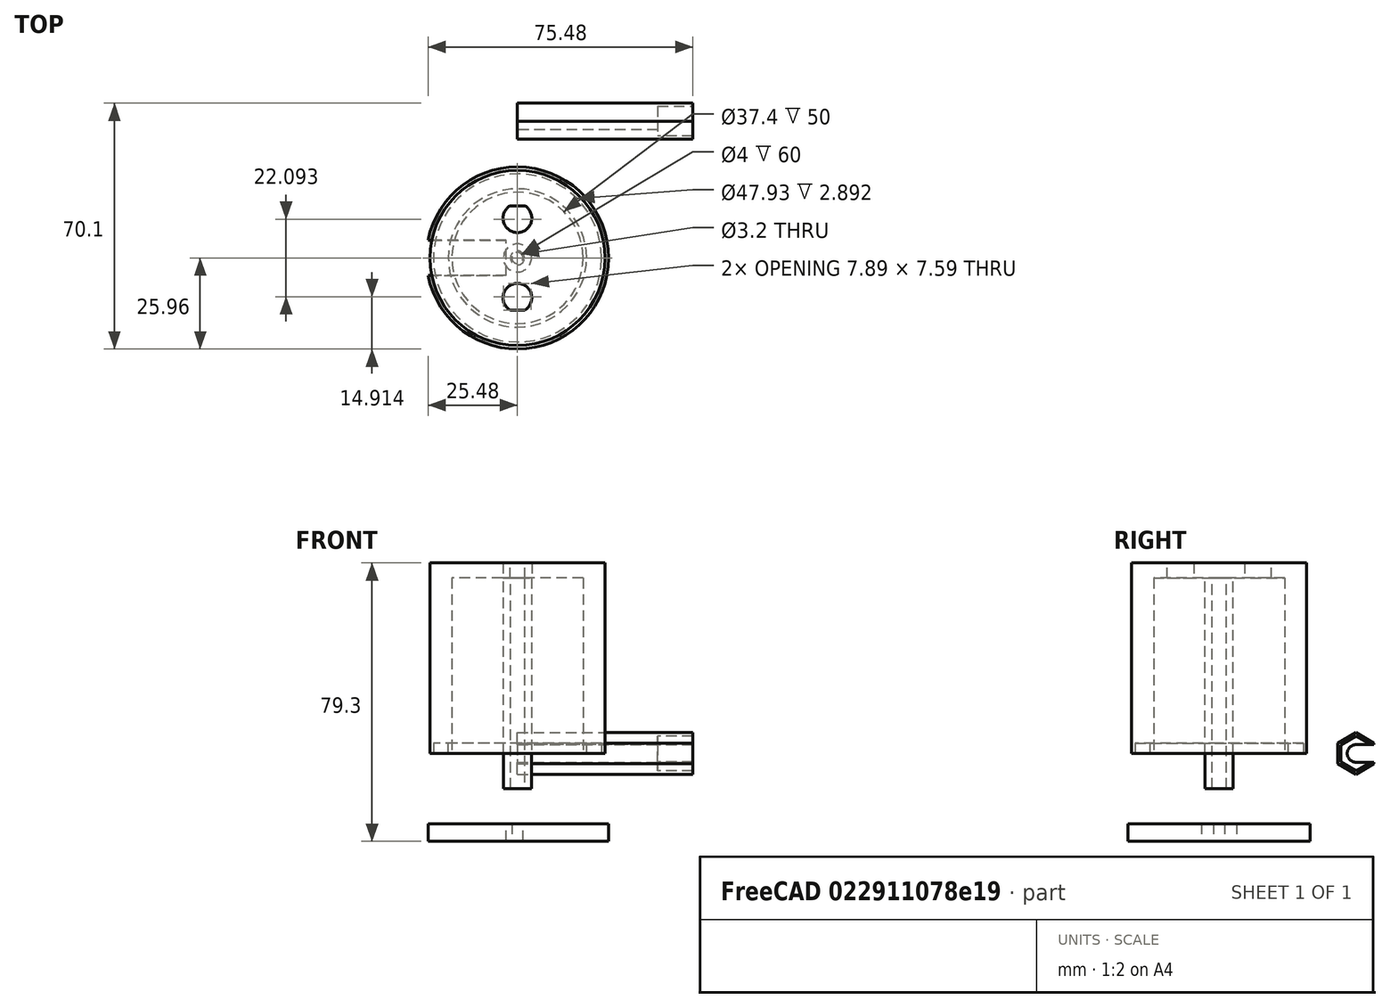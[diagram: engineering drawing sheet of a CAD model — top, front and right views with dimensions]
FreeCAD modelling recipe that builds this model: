
FCSTD DOCUMENT  (FreeCAD 0.18.4R)
Label: sealedadaptor
License: All rights reserved
LicenseURL: http://en.wikipedia.org/wiki/All_rights_reserved
objects: TechDraw::DrawViewDimension×10, Sketcher::SketchObject×8, Spreadsheet::Sheet×6, TechDraw::DrawViewPart×6, PartDesign::Pocket×4, PartDesign::Plane×3, PartDesign::Pad×3, PartDesign::Body×3, Part::Feature×2, PartDesign::Revolution×1, PartDesign::PolarPattern×1, TechDraw::DrawSVGTemplate×1, TechDraw::DrawViewAnnotation×1, TechDraw::DrawPage×1
note: 33 computed .brp shape members not serialized (recipe doc carries the construction recipe); baked Part::Feature solids carry a one-line shape summary decoded from their .brp

FEATURE [Spreadsheet::Sheet] Spreadsheet  label="conn"
  cells = A1=cutout_diam; B1==8mm; A2=cutout_slot_offset; B2==3.6mm; A3=separation; B3==conn.B5 + 1mm; A4=x_shift; B4==22.23mm - 13.97mm; A5=max_diam; B5==12.7mm; A6=max_thick; B6==4.3mm; A7=offset_from_wall; B7==1mm; A8=number connectors; B8=2
FEATURE [Spreadsheet::Sheet] Spreadsheet001  label="oring"
  cells = A1=gland_width; B1==0.16 * 25.4mm; C1=Oring #223; A2=gland_depth; B2==0.106 * 25.4mm; A3=gland_OD; B3==1.887 * 25.4mm
FEATURE [Spreadsheet::Sheet] Spreadsheet002  label="dimz"
  cells = A1=nutspace_height; B1==15mm; A2=nutspace_width; B2==0.4 * 25.4mm; A3=Screw diam; B3==0.25 * 25.4mm + 1mm; A4=box_height; B4==50mm; A5=oring_wall; B5==1mm; A6=plate_thick; B6==5mm; A9=track_width; B9==10mm; A11=internal_diameter; B11==oring.B3 / 2 - oring.B1 - dimz.B5; A12=screwpillar_overextent; B12==10mm; A13=insert hole diam; B13==4mm; A14=separate insert pilars; B14==12mm; A16=screw_hole_bottomdiam; B16==3.2mm
FEATURE [Sketcher::SketchObject] Sketch  label="oring and base struct"
  MapMode = 5
  Placement = pos=(0,0,0) rot=(1,0,0;1.5708rad)
  Support = -> [XZ_Plane]
  expr: Constraints[27] = dimz.B4
  expr: Constraints[29] = conn.B6
  expr: Constraints[26] = dimz.B5
  expr: Constraints[28] = oring.B3 / 2
  expr: Constraints[25] = oring.B2 + tol.B1
  expr: Constraints[24] = oring.B1 + tol.B1
  sketch-geometry (10):
    g0: LineSegment StartX=0 StartY=54.3 StartZ=0 EndX=0 EndY=50 EndZ=0
    g1: LineSegment StartX=0 StartY=50 StartZ=0 EndX=18.7009 EndY=50 EndZ=0
    g2: LineSegment StartX=18.7009 StartY=50 StartZ=0 EndX=18.7009 EndY=0 EndZ=0
    g3: LineSegment StartX=18.7009 StartY=0 StartZ=0 EndX=19.7009 EndY=0 EndZ=0
    g4: LineSegment StartX=19.7009 StartY=0 StartZ=0 EndX=19.7009 EndY=2.8924 EndZ=0
    g5: LineSegment StartX=19.7009 StartY=2.8924 StartZ=0 EndX=23.9649 EndY=2.8924 EndZ=0
    g6: LineSegment StartX=23.9649 StartY=2.8924 StartZ=0 EndX=23.9649 EndY=0 EndZ=0
    g7: LineSegment StartX=23.9649 StartY=0 StartZ=0 EndX=24.9649 EndY=0 EndZ=0
    g8: LineSegment StartX=24.9649 StartY=0 StartZ=0 EndX=24.9649 EndY=54.3 EndZ=0
    g9: LineSegment StartX=24.9649 StartY=54.3 StartZ=0 EndX=0 EndY=54.3 EndZ=0
  constraints (30):
    c: Coincident(g0,g1)
    c: Coincident(g1,g2)
    c: Coincident(g2,g3)
    c: Coincident(g3,g4)
    c: Coincident(g4,g5)
    c: Coincident(g5,g6)
    c: Coincident(g6,g7)
    c: Coincident(g7,g8)
    c: Coincident(g8,g9)
    c: Coincident(g9,g0)
    c: Parallel(g0,g2)
    c: Parallel(g2,g4)
    c: Parallel(g4,g6)
    c: Parallel(g6,g8)
    c: Parallel(g8,g-2)
    c: Parallel(g1,g9)
    c: Parallel(g9,g5)
    c: Parallel(g5,g3)
    c: Parallel(g3,g7)
    c: Parallel(g3,g-1)
    c: PointOnObject(g0,g-2)
    c: PointOnObject(g2,g-1)
    c: Equal(g7,g3)
    c: Equal(g6,g4)
    c: DistanceX(g5,g5) = 4.264
    c: DistanceY(g4,g4) = 2.8924
    c: DistanceX(g3,g3) = 1
    c: DistanceY(g-1,g0) = 50
    c: DistanceX(g-1,g6) = 23.9649
    c: DistanceY(g0,g0) = 4.3
FEATURE [PartDesign::Revolution] Revolution  label="base_structure"
  Angle = 360
  Axis = (0,-2e-16,1)
  Base = (0,0,0)
  Placement = pos=(0,0,0) rot=(1,0,0;1.5708rad)
  Profile = -> Sketch
  ReferenceAxis = -> Sketch [V_Axis]
  Reversed = true
FEATURE [Spreadsheet::Sheet] Spreadsheet003  label="tol"
  cells = A1=inplane; B1==0.2mm
FEATURE [PartDesign::Plane] DatumPlane  label="bottom_face"
  AttachmentOffset = pos=(0,0,-50) rot=(0,0,1;0rad)
  Length = 59.9158
  MapMode = 3
  Placement = pos=(0,1.11e-14,50) rot=(1,0,0;3.14159rad)
  ResizeMode = 0
  Support = -> [Revolution]
  Width = 59.9158
  expr: AttachmentOffset.Base.z = -dimz.B4
FEATURE [Sketcher::SketchObject] Sketch001  label="cutout_conn"
  MapMode = 5
  Placement = pos=(0,1.11e-14,50) rot=(1,0,0;3.14159rad)
  Support = -> [DatumPlane]
  expr: Constraints[6] = dimz.B11 - conn.B5 / 2 - tol.B1 - conn.B7
  expr: Constraints[5] = 360deg - acos(conn.B2 / conn.B1)
  expr: Constraints[4] = conn.B1 / 2 + tol.B1 / 2
  sketch-geometry (2):
    g0: ArcOfCircle CenterX=0 CenterY=11.3509 CenterZ=0 NormalX=0 NormalY=0 NormalZ=1 AngleXU=0 Radius=4.1 StartAngle=2.12281 EndAngle=7.30197
    g1: LineSegment StartX=-2.15006 StartY=14.8419 StartZ=0 EndX=2.15006 EndY=14.8419 EndZ=0
  constraints (7):
    c: Coincident(g1,g0)
    c: Coincident(g1,g0)
    c: PointOnObject(g0,g-2)
    c: Perpendicular(g-2,g1)
    c: Radius(g0) = 4.1
    c: Angle(g0) = 5.17915
    c: DistanceY(g-1,g0) = 11.3509
FEATURE [PartDesign::Pocket] Pocket  label="conn_hole"
  BaseFeature = -> Revolution
  Length = 5
  Length2 = 100
  Placement = pos=(0,0,0) rot=(1,0,0;1.5708rad)
  Profile = -> Sketch001
  Type = 1
FEATURE [PartDesign::PolarPattern] PolarPattern  label="repeating_connholes"
  Angle = 360
  Axis = -> Sketch001 [N_Axis]
  BaseFeature = -> Pocket
  Occurrences = 2
  Originals = -> [Pocket]
  Placement = pos=(0,0,0) rot=(1,0,0;1.5708rad)
  expr: Occurrences = conn.B8
FEATURE [Sketcher::SketchObject] Sketch002
  MapMode = 5
  Placement = pos=(0,1.11e-14,50) rot=(1,0,0;3.14159rad)
  Support = -> [DatumPlane]
  expr: Constraints[4] = 0
  expr: Constraints[3] = dimz.B13 / 2
  expr: Constraints[1] = dimz.B13
  sketch-geometry (2):
    g0: Circle CenterX=0 CenterY=0 CenterZ=0 NormalX=0 NormalY=0 NormalZ=1 AngleXU=0 Radius=4
    g1: Circle CenterX=0 CenterY=0 CenterZ=0 NormalX=0 NormalY=0 NormalZ=1 AngleXU=0 Radius=2
  constraints (5):
    c: PointOnObject(g0,g-1)
    c: Radius(g0) = 4
    c: Coincident(g1,g0)
    c: Radius(g1) = 2
    c: DistanceX(g-1,g0) = 0
FEATURE [PartDesign::Pad] Pad  label="screw_pillar"
  BaseFeature = -> PolarPattern
  Length = 60
  Length2 = 100
  Placement = pos=(0,0,0) rot=(1,0,0;1.5708rad)
  Profile = -> Sketch002
  Type = 0
  expr: Length = dimz.B4 + dimz.B12
FEATURE [PartDesign::Body] Body  label="top"
  Group = -> [Sketch,Revolution,DatumPlane,Sketch001,Pocket,PolarPattern,Sketch002,Pad]
  Origin = -> Origin
  Tip = -> Pad
FEATURE [Part::Feature] Part__Feature  label="connector1"
  Placement = pos=(0,11.3509,41.74) rot=(0,-1,0;1.5708rad)
  shape: bbox 12.7 x 12.7 x 22.23 mm, 134 faces, 0 solids (baked)
  expr: Placement.Base.y = dimz.B11 - conn.B5 / 2 - tol.B1 - conn.B7
  expr: Placement.Base.z = dimz.B4 - (22.23mm - 13.97mm)
FEATURE [Part::Feature] Part__Feature001  label="connector2"
  Placement = pos=(0,-11.3509,41.74) rot=(0,-1,0;1.5708rad)
  shape: bbox 12.7 x 12.7 x 22.23 mm, 134 faces, 0 solids (baked)
  expr: Placement.Base.y = -(dimz.B11 - conn.B5 / 2 - tol.B1 - conn.B7)
  expr: Placement.Base.z = dimz.B4 - (22.23mm - 13.97mm)
FEATURE [Sketcher::SketchObject] Sketch003
  MapMode = 5
  Support = -> [XY_Plane001]
  expr: Constraints[0] = oring.B3 / 2 + 2 * dimz.B5
  sketch-geometry (1):
    g0: Circle CenterX=0 CenterY=0 CenterZ=0 NormalX=0 NormalY=0 NormalZ=1 AngleXU=0 Radius=25.9649
  constraints (2):
    c: Radius(g0) = 25.9649
    c: Coincident(g-1,g0)
FEATURE [PartDesign::Pad] Pad001
  Length = 5
  Length2 = 100
  Profile = -> Sketch003
  Type = 0
  expr: Length = dimz.B6
FEATURE [Sketcher::SketchObject] Sketch004
  MapMode = 5
  Placement = pos=(0,0,0) rot=(1,0,0;3.14159rad)
  Support = -> [Pad001]
  expr: Constraints[11] = dimz.B16
  expr: Constraints[9] = dimz.B9
  expr: Constraints[12] = oring.B3 / 2 + oring.B1 + 2 * dimz.B5
  expr: Constraints[1] = dimz.B16 / 2
  sketch-geometry (5):
    g0: Circle CenterX=0 CenterY=0 CenterZ=0 NormalX=0 NormalY=0 NormalZ=1 AngleXU=0 Radius=1.6
    g1: LineSegment StartX=-30.0289 StartY=5 StartZ=0 EndX=-3.2 EndY=5 EndZ=0
    g2: LineSegment StartX=-3.2 StartY=5 StartZ=0 EndX=-3.2 EndY=-5 EndZ=0
    g3: LineSegment StartX=-3.2 StartY=-5 StartZ=0 EndX=-30.0289 EndY=-5 EndZ=0
    g4: LineSegment StartX=-30.0289 StartY=-5 StartZ=0 EndX=-30.0289 EndY=5 EndZ=0
  constraints (13):
    c: Coincident(g0,g-1)
    c: Radius(g0) = 1.6
    c: Coincident(g1,g2)
    c: Coincident(g2,g3)
    c: Coincident(g3,g4)
    c: Coincident(g4,g1)
    c: Horizontal(g1)
    c: Horizontal(g3)
    c: Vertical(g4)
    c: DistanceY(g2,g2) = 10
    c: Symmetric(g1,g2,g-1)
    c: DistanceX(g1,g-1) = 3.2
    c: DistanceX(g3,g-1) = 30.0289
FEATURE [PartDesign::Pocket] Pocket001
  BaseFeature = -> Pad001
  Length = 5
  Length2 = 100
  Profile = -> Sketch004
  Type = 1
FEATURE [PartDesign::Body] Body001  label="bottom"
  Group = -> [Sketch003,Pad001,Sketch004,Pocket001]
  Origin = -> Origin001
  Placement = pos=(0,0,-25) rot=(0,0,1;0rad)
  Tip = -> Pocket001
FEATURE [TechDraw::DrawSVGTemplate] Template
  EditableTexts = Designed_by_Name=Félix Thouin; Drawing_number=1; FC-Date=2021-02-09; FC-SC=1; FC-SH=1; FC-Title=Sealed adapter; Subtitle=For FTIR signal feedthrough; Weight=30g
  Height = 210
  Orientation = 1
  Width = 297
FEATURE [TechDraw::DrawViewPart] View
  CoarseView = false
  Direction = (1,0,0)
  Focus = 100
  HardHidden = false
  IsoCount = 0
  IsoHidden = false
  IsoVisible = false
  LockPosition = false
  Perspective = false
  Rotation = 0
  ScaleType = 0
  SeamHidden = false
  SeamVisible = false
  SmoothHidden = false
  SmoothVisible = false
  Source = -> [Body]
  X = 52.5647
  Y = 150.576
FEATURE [TechDraw::DrawViewPart] View001
  CoarseView = false
  Direction = (0,0,-1)
  Focus = 100
  HardHidden = false
  IsoCount = 0
  IsoHidden = false
  IsoVisible = false
  LockPosition = false
  Perspective = false
  Rotation = 0
  ScaleType = 0
  SeamHidden = false
  SeamVisible = false
  SmoothHidden = false
  SmoothVisible = false
  Source = -> [Body]
  X = 126.594
  Y = 154.604
FEATURE [TechDraw::DrawViewPart] View002
  CoarseView = false
  Direction = (0.354,-0.354,-0.866)
  Focus = 100
  HardHidden = false
  IsoCount = 0
  IsoHidden = false
  IsoVisible = false
  LockPosition = false
  Perspective = false
  Rotation = 0
  ScaleType = 0
  SeamHidden = false
  SeamVisible = false
  SmoothHidden = false
  SmoothVisible = false
  Source = -> [Body]
  X = 215.73
  Y = 153.597
FEATURE [Sketcher::SketchObject] Sketch008
  MapMode = 5
  Placement = pos=(0,0,0) rot=(0.57735,0.57735,0.57735;2.0944rad)
  Support = -> [YZ_Plane002]
  expr: Constraints[19] = (dimztool.B2 + tol.B1 + dimztool.B3) / 2
  sketch-geometry (7):
    g0: LineSegment StartX=5.13986 StartY=-2.9675 StartZ=0 EndX=5.13986 EndY=2.9675 EndZ=0
    g1: LineSegment StartX=5.13986 StartY=2.9675 StartZ=0 EndX=0 EndY=5.935 EndZ=0
    g2: LineSegment StartX=0 StartY=5.935 StartZ=0 EndX=-5.13986 EndY=2.9675 EndZ=0
    g3: LineSegment StartX=-5.13986 StartY=2.9675 StartZ=0 EndX=-5.13986 EndY=-2.9675 EndZ=0
    g4: LineSegment StartX=-5.13986 StartY=-2.9675 StartZ=0 EndX=0 EndY=-5.935 EndZ=0
    g5: LineSegment StartX=-4e-16 StartY=-5.935 StartZ=0 EndX=5.13986 EndY=-2.9675 EndZ=0
    g6: Circle [constr] CenterX=0 CenterY=0 CenterZ=0 NormalX=0 NormalY=0 NormalZ=1 AngleXU=0 Radius=5.935
  constraints (16):
    c: Coincident(g0,g1)
    c: Coincident(g1,g2)
    c: Coincident(g2,g3)
    c: Coincident(g3,g4)
    c: Coincident(g4,g5)
    c: Coincident(g5,g0)
    c: Equal(g0, g1-g5) x5
    c: PointOnObject(g0,g6)
    c: PointOnObject(g1,g6)
    c: PointOnObject(g2,g6)
    c: PointOnObject(g3,g6)
    c: PointOnObject(g4,g6)
    c: PointOnObject(g5,g6)
    c: Coincident(g6,g-1)
    c: PointOnObject(g1,g-2)
    c: Radius(g6) = 5.935
FEATURE [Spreadsheet::Sheet] Spreadsheet004  label="dimztool"
  cells = A1=height; B1==50mm; A2=sma_dist_apex; B2==9.67mm; A3=extra_thick; B3==2mm; A4=depth; B4==10mm; A5=cable_diam; B5==5mm
FEATURE [PartDesign::Pad] Pad002
  Length = 50
  Length2 = 100
  Placement = pos=(0,0,0) rot=(0.57735,0.57735,0.57735;2.0944rad)
  Profile = -> Sketch008
  Type = 0
  expr: Length = dimztool.B1
FEATURE [Spreadsheet::Sheet] Spreadsheet005  label="tol001"
  cells = A1=in plane tol; B1==0.2mm
FEATURE [PartDesign::Plane] DatumPlane002  label="cabletrench_datum"
  Length = 24
  MapMode = 2
  Placement = pos=(0,0,0) rot=(0.57735,0.57735,0.57735;2.0944rad)
  ResizeMode = 0
  Support = -> [Pad002]
  Width = 24
FEATURE [Sketcher::SketchObject] Sketch009
  MapMode = 5
  Placement = pos=(0,0,0) rot=(0.57735,0.57735,0.57735;2.0944rad)
  Support = -> [DatumPlane002]
  expr: Constraints[10] = dimztool.B5
  expr: Constraints[7] = dimztool.B5 / 2
  sketch-geometry (4):
    g0: ArcOfCircle CenterX=0 CenterY=0 CenterZ=0 NormalX=0 NormalY=0 NormalZ=1 AngleXU=0 Radius=2.5 StartAngle=1.5708 EndAngle=4.71239
    g1: LineSegment StartX=2.22264e-08 StartY=2.5 StartZ=0 EndX=9.19793 EndY=2.5 EndZ=0
    g2: LineSegment StartX=9.19793 StartY=2.5 StartZ=0 EndX=9.19793 EndY=-2.5 EndZ=0
    g3: LineSegment StartX=9.19793 StartY=-2.5 StartZ=0 EndX=2.22264e-08 EndY=-2.5 EndZ=0
  constraints (11):
    c: Coincident(g0,g-1)
    c: Coincident(g1,g2)
    c: Coincident(g2,g3)
    c: Coincident(g1,g0)
    c: Coincident(g3,g0)
    c: Parallel(g1,g-1)
    c: Parallel(g3,g-1)
    c: Radius(g0) = 2.5
    c: DistanceX(g0,g0) = 0
    c: Symmetric(g2,g1,g-1)
    c: DistanceY(g2,g2) = 5
FEATURE [PartDesign::Pocket] Pocket005  label="cabletrench"
  BaseFeature = -> Pad002
  Length = 5
  Length2 = 100
  Placement = pos=(0,0,0) rot=(0.57735,0.57735,0.57735;2.0944rad)
  Profile = -> Sketch009
  Reversed = true
  Type = 1
FEATURE [PartDesign::Plane] DatumPlane003  label="wrench_datum"
  AttachmentOffset = pos=(0,0,50) rot=(0,0,1;0rad)
  Length = 24
  MapMode = 2
  Placement = pos=(50,0,0) rot=(0.57735,0.57735,0.57735;2.0944rad)
  ResizeMode = 0
  Support = -> [Pocket005]
  Width = 24
  expr: AttachmentOffset.Base.z = dimztool.B1
FEATURE [Sketcher::SketchObject] Sketch010
  MapMode = 5
  Placement = pos=(50,0,0) rot=(0.57735,0.57735,0.57735;2.0944rad)
  Support = -> [DatumPlane003]
  expr: Constraints[19] = dimztool.B2 + tol.B1
  sketch-geometry (7):
    g0: LineSegment StartX=4.27384 StartY=2.4675 StartZ=0 EndX=0 EndY=4.935 EndZ=0
    g1: LineSegment StartX=0 StartY=4.935 StartZ=0 EndX=-4.27384 EndY=2.4675 EndZ=0
    g2: LineSegment StartX=-4.27384 StartY=2.4675 StartZ=0 EndX=-4.27384 EndY=-2.4675 EndZ=0
    g3: LineSegment StartX=-4.27384 StartY=-2.4675 StartZ=0 EndX=0 EndY=-4.935 EndZ=0
    g4: LineSegment StartX=0 StartY=-4.935 StartZ=0 EndX=4.27384 EndY=-2.4675 EndZ=0
    g5: LineSegment StartX=4.27384 StartY=-2.4675 StartZ=0 EndX=4.27384 EndY=2.4675 EndZ=0
    g6: Circle [constr] CenterX=0 CenterY=0 CenterZ=0 NormalX=0 NormalY=0 NormalZ=1 AngleXU=0 Radius=4.935
  constraints (16):
    c: Coincident(g0,g1)
    c: Coincident(g1,g2)
    c: Coincident(g2,g3)
    c: Coincident(g3,g4)
    c: Coincident(g4,g5)
    c: Coincident(g5,g0)
    c: Equal(g0, g1-g5) x5
    c: PointOnObject(g0,g6)
    c: PointOnObject(g1,g6)
    c: PointOnObject(g2,g6)
    c: PointOnObject(g3,g6)
    c: PointOnObject(g4,g6)
    c: PointOnObject(g5,g6)
    c: Coincident(g6,g-1)
    c: PointOnObject(g0,g-2)
    c: Distance(g0,g3) = 9.87
FEATURE [PartDesign::Pocket] Pocket006
  BaseFeature = -> Pocket005
  Length = 10
  Length2 = 100
  Placement = pos=(0,0,0) rot=(0.57735,0.57735,0.57735;2.0944rad)
  Profile = -> Sketch010
  Type = 0
  expr: Length = dimztool.B4
FEATURE [PartDesign::Body] Body002  label="tool"
  Group = -> [Sketch008,Pad002,DatumPlane002,Sketch009,Pocket005,DatumPlane003,Sketch010,Pocket006]
  Origin = -> Origin002
  Placement = pos=(0,39,0) rot=(0,0,1;0rad)
  Tip = -> Pocket006
FEATURE [TechDraw::DrawViewPart] View003
  CoarseView = false
  Direction = (0,0.5,-0.866)
  Focus = 100
  HardHidden = false
  IsoCount = 0
  IsoHidden = false
  IsoVisible = false
  LockPosition = false
  Perspective = false
  Rotation = 0
  ScaleType = 0
  SeamHidden = false
  SeamVisible = false
  SmoothHidden = false
  SmoothVisible = false
  Source = -> [Pocket006]
  X = 189.291
  Y = 81.3309
FEATURE [TechDraw::DrawViewPart] View004
  CoarseView = false
  Direction = (1,0,0)
  Focus = 100
  HardHidden = false
  IsoCount = 0
  IsoHidden = false
  IsoVisible = false
  LockPosition = false
  Perspective = false
  Rotation = 0
  ScaleType = 0
  SeamHidden = false
  SeamVisible = false
  SmoothHidden = false
  SmoothVisible = false
  Source = -> [Body002]
  X = 233.356
  Y = 81.3309
FEATURE [TechDraw::DrawViewPart] View005
  CoarseView = false
  Direction = (0,0,-1)
  Focus = 100
  HardHidden = false
  IsoCount = 0
  IsoHidden = false
  IsoVisible = false
  LockPosition = false
  Perspective = false
  Rotation = 0
  ScaleType = 0
  SeamHidden = false
  SeamVisible = false
  SmoothHidden = false
  SmoothVisible = false
  Source = -> [Pocket001]
  X = 63.1403
  Y = 55.1439
FEATURE [TechDraw::DrawViewDimension] Dimension
  Arbitrary = false
  FormatSpec = %.2f
  LockPosition = false
  MeasureType = 1
  OverTolerance = 0
  References2D = -> [View]
  Rotation = 0
  ScaleType = 0
  Type = 2
  UnderTolerance = 0
  X = 9.28777
  Y = -42.7615
FEATURE [TechDraw::DrawViewDimension] Dimension001
  Arbitrary = false
  FormatSpec = ⌀%.2f
  LockPosition = false
  MeasureType = 1
  OverTolerance = 0
  References2D = -> [View001]
  Rotation = 0
  ScaleType = 0
  Type = 5
  UnderTolerance = 0
  X = 37.7698
  Y = 14.3525
FEATURE [TechDraw::DrawViewDimension] Dimension002
  Arbitrary = false
  FormatSpec = ⌀%.2f
  LockPosition = false
  MeasureType = 1
  OverTolerance = 0
  References2D = -> [View001]
  Rotation = 0
  ScaleType = 0
  Type = 5
  UnderTolerance = 0
  X = 39.2806
  Y = -13.8489
FEATURE [TechDraw::DrawViewDimension] Dimension003
  Arbitrary = false
  FormatSpec = ⌀%.2f
  LockPosition = false
  MeasureType = 1
  OverTolerance = 0
  References2D = -> [View001]
  Rotation = 0
  ScaleType = 0
  Type = 5
  UnderTolerance = 0
  X = -33.741
  Y = -2.01439
FEATURE [TechDraw::DrawViewDimension] Dimension004
  Arbitrary = false
  FormatSpec = %.2f
  LockPosition = false
  MeasureType = 1
  OverTolerance = 0
  References2D = -> [View001]
  Rotation = 0
  ScaleType = 0
  Type = 1
  UnderTolerance = 0
  X = 37.4444
  Y = 8.56115
FEATURE [TechDraw::DrawViewDimension] Dimension005
  Arbitrary = false
  FormatSpec = %.2f
  LockPosition = false
  MeasureType = 1
  OverTolerance = 0
  References2D = -> [View001]
  Rotation = 0
  ScaleType = 0
  Type = 1
  UnderTolerance = 0
  X = 41.3354
  Y = -0.503597
FEATURE [TechDraw::DrawViewDimension] Dimension006
  Arbitrary = false
  FormatSpec = ⌀%.2f
  LockPosition = false
  MeasureType = 1
  OverTolerance = 0
  References2D = -> [View001]
  Rotation = 0
  ScaleType = 0
  Type = 5
  UnderTolerance = 0
  X = -40.5396
  Y = -5.03597
FEATURE [TechDraw::DrawViewDimension] Dimension007
  Arbitrary = false
  FormatSpec = %.2f
  LockPosition = false
  MeasureType = 1
  OverTolerance = 0
  References2D = -> [View]
  Rotation = 0
  ScaleType = 0
  Type = 2
  UnderTolerance = 0
  X = 16.6555
  Y = 3.48921
FEATURE [TechDraw::DrawViewAnnotation] Annotation
  Font = osifont
  LineSpace = 80
  LockPosition = false
  MaxWidth = -1
  Rotation = 0
  ScaleType = 0
  Text = For Oring size 223 | M3 screw | M3 heat set insert at center pillar | Tool for SMA plug | For Vertex 70 FTIR
  TextSize = 3
  TextStyle = 0
  X = 125.083
  Y = 98.2014
FEATURE [TechDraw::DrawViewDimension] Dimension008
  Arbitrary = false
  FormatSpec = %.2f
  LockPosition = false
  MeasureType = 1
  OverTolerance = 0
  References2D = -> [View003]
  Rotation = 0
  ScaleType = 0
  Type = 1
  UnderTolerance = 0
  X = -2.26619
  Y = 17.2305
FEATURE [TechDraw::DrawViewDimension] Dimension009
  Arbitrary = false
  FormatSpec = R%.2f
  LockPosition = false
  MeasureType = 1
  OverTolerance = 0
  References2D = -> [View004]
  Rotation = 0
  ScaleType = 0
  Type = 4
  UnderTolerance = 0
  X = 2.76978
  Y = 17.8777
FEATURE [TechDraw::DrawPage] Page  label="TechDrawing"
  KeepUpdated = true
  ProjectionType = 0
  Template = -> Template
  Views = -> [View,View001,View002,View003,View004,View005,Dimension,Dimension001,Dimension002,Dimension003,Dimension004,Dimension005,Dimension006,Dimension007,Annotation,Dimension008,Dimension009]
